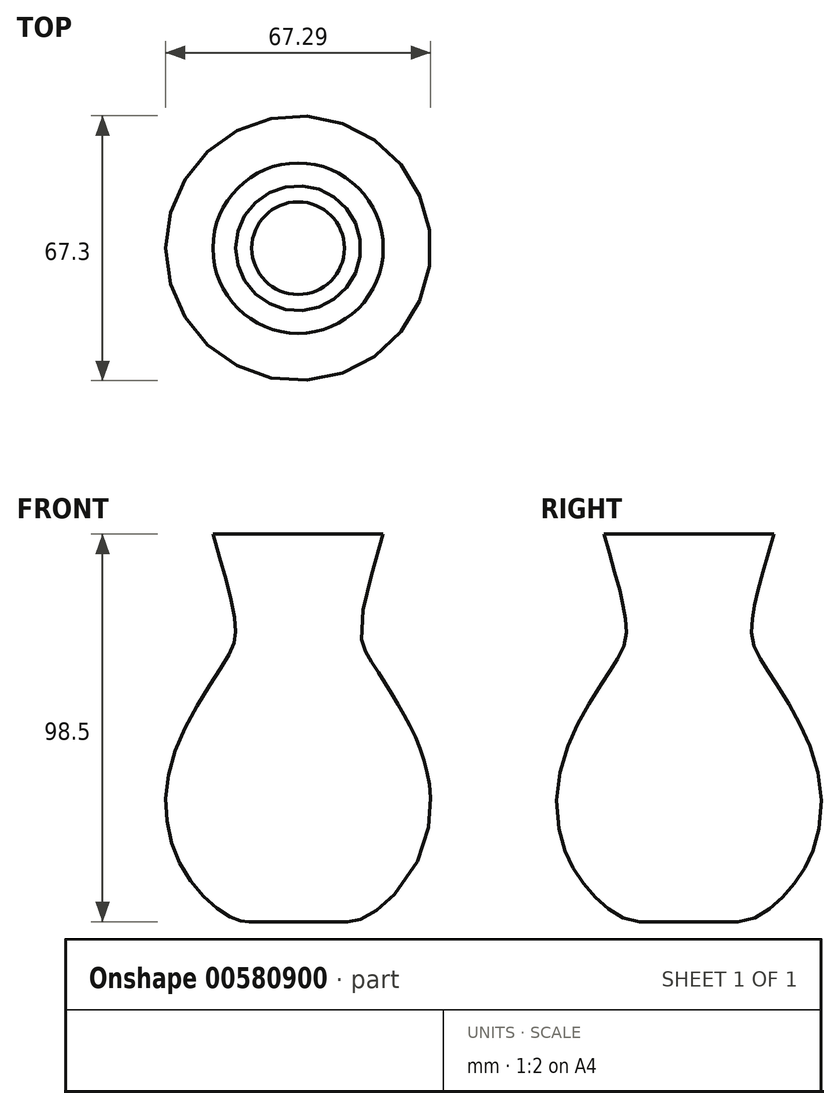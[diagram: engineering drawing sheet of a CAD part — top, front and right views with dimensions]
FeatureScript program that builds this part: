
annotation { "Feature Type Name" : "Feature", "Feature Type Description" : "" }
export const myFeature = defineFeature(function(context is Context, id is Id, definition is map)
    precondition{}
    {
        {
            var Q0;
            Q0=qCreatedBy(makeId("Front.planeOp"),FACE);
            var sketch = newSketch(context, id + "F0", { "sketchPlane" : qUnion([Q0])});
            skFitSpline(sketch, "E0", {"points": [v(21.64, 51.14) * mm, v(15.9, 27.5) * mm, v(18.2, 19.46) * mm, v(32.2, -6.94) * mm, v(28.98, -34.5) * mm, v(16.13, -46.66) * mm, v(11.77, -47.35) * mm], "startDerivative": vector(-41.12, -138.37) * mm, "endDerivative": vector(-45.62, 0.99) * mm});
            skLineSegment(sketch, "E1", {"start": v(13.05, -47.38) * mm, "end": v(0, -47.38) * mm});
            skLineSegment(sketch, "E2", {"start": v(0, 58.03) * mm, "end": v(0, -39.55) * mm, "construction": true});
            skSolve(sketch);
        }
        {
            var Q0;
            Q0=sQuery(id+"F0.wireOp",EDGE,"E2");
            var Q1;
            Q1=sQuery(id+"F0.wireOp",EDGE,"E0");
            var Q2;
            Q2=sQuery(id+"F0.wireOp",EDGE,"E2");
            revolve(context, id + "F1", {"bodyType" : ToolBodyType.SURFACE, "surfaceEntities" : qUnion([Q0, Q1]), "axis" : qUnion([Q2]), "revolveType" : RevolveType.FULL});
        }
    });
